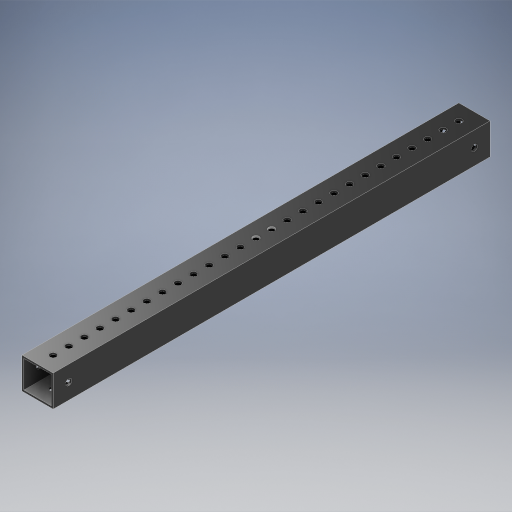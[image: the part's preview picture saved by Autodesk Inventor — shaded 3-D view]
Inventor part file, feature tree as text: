
AUTODESK INVENTOR PART (.ipt)
format: ipt  version: 2024.2 (Build 282272000, 272)  size: 792,576 bytes
history: native  units: in
note: dims shown in document units (in); Inventor stores cm internally (conversion verified against a paired STEP export)
features: other x13, extrude x9, hole x3, pattern_linear x3, mirror x3, sheet_metal_op x1, plane x1
ambient origin geometry x8: Origin, YZ Plane, XZ Plane, XY Plane, X Axis, Y Axis, Z Axis, Center Point
bodies: Solid1 (feature_tree)
feature tree (33):
  other  "Blocks"
  other  "Base Sketch"
  extrude  "Base"  Depth=1.0in
  extrude  "MAX Corner"  Depth=1.0in
  extrude  "MAX Corner Cut"  Depth=0.0625in
  extrude  "Scribe Lines"  Depth=0.0625in
  other  "Side Middle"
  other  "Top Middle"
  other  "Side Holes Sketch"
  hole  "Top Side Hole"  [1 undecoded]
  hole  "Mid Side Hole"  [1 undecoded]
  hole  "Btm Side Hole"  [1 undecoded]
  pattern_linear  "Side Holes"  Spacing1=0.04in  [1 undecoded]
  mirror  "Side Mirror"
  extrude  "MAXTube Hole"  Depth=0.04in
  extrude  "MAXTube Outside"  Depth=14.0in
  pattern_linear  "MAXTube Pattern"  Spacing1=0.0in  [1 undecoded]
  mirror  "MAXTube Mirror"
  extrude  "Left Top Hole"  Depth=14.0in
  extrude  "Mid Top Hole"  TaperAngle=0.0deg  [1 undecoded]
  extrude  "Right Top Hole"  TaperAngle=0.0deg  [1 undecoded]
  pattern_linear  "Top Holes"  Spacing1=0.005in  [1 undecoded]
  mirror  "Top Mirror"
  sheet_metal_op  "Corner"
  other  "MAXTube"
  plane  "Work Plane3"
  other  "Corner:5"
  other  "Corner:6"
  other  "Corner:7"
  other  "Corner:8"
  other  "MAXTube:1"
  other  "MAXTube:2"
  other  "MAXTube:3"
note: 8 required parameter values undecoded (feature->parameter linkage not recoverable at this tier; creation-order binding heuristic only, values carry confidence <= 0.55)
